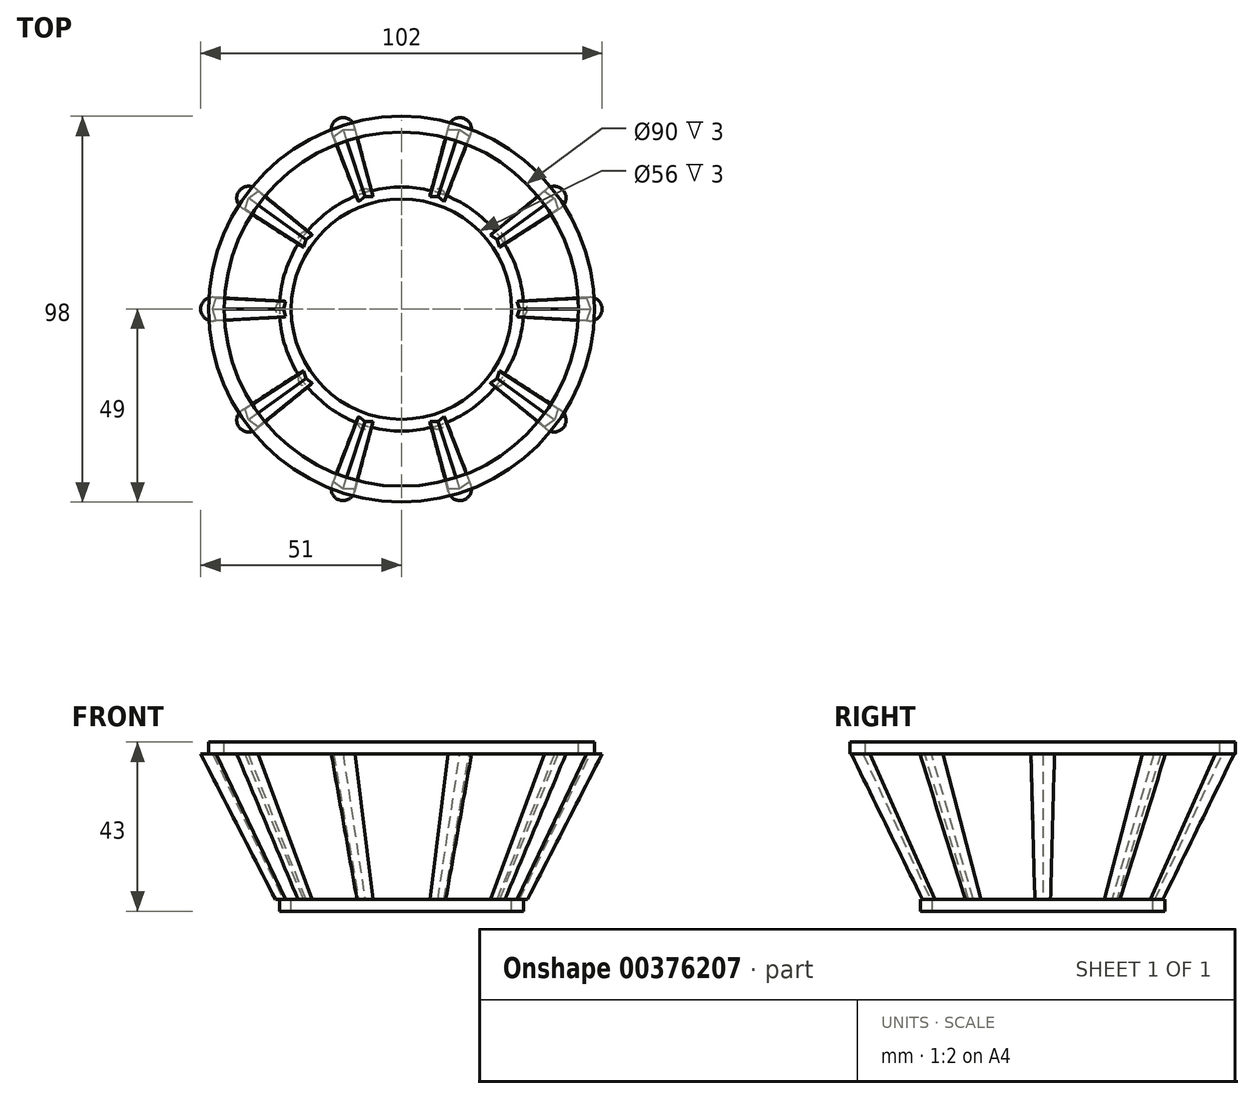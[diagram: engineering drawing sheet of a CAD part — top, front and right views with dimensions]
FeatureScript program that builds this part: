
annotation { "Feature Type Name" : "Feature", "Feature Type Description" : "" }
export const myFeature = defineFeature(function(context is Context, id is Id, definition is map)
    precondition{}
    {
        {
            var Q0;
            Q0=qCreatedBy(makeId("Top.planeOp"),FACE);
            var sketch = newSketch(context, id + "F0", { "sketchPlane" : qUnion([Q0])});
            skCircle(sketch, "E0.cCircle", {"center": v(0, 0) * mm, "radius": 48 * mm, "construction": true});
            skLineSegment(sketch, "E0.0", {"start": v(48, 0) * mm, "end": v(38.83, -28.21) * mm});
            skLineSegment(sketch, "E0.1", {"start": v(38.83, -28.21) * mm, "end": v(14.83, -45.65) * mm});
            skLineSegment(sketch, "E0.2", {"start": v(14.83, -45.65) * mm, "end": v(-14.83, -45.65) * mm});
            skLineSegment(sketch, "E0.3", {"start": v(-14.83, -45.65) * mm, "end": v(-38.83, -28.21) * mm});
            skLineSegment(sketch, "E0.4", {"start": v(-38.83, -28.21) * mm, "end": v(-48, 0) * mm});
            skLineSegment(sketch, "E0.5", {"start": v(-48, 0) * mm, "end": v(-38.83, 28.21) * mm});
            skLineSegment(sketch, "E0.6", {"start": v(-38.83, 28.21) * mm, "end": v(-14.83, 45.65) * mm});
            skLineSegment(sketch, "E0.7", {"start": v(-14.83, 45.65) * mm, "end": v(14.83, 45.65) * mm});
            skLineSegment(sketch, "E0.8", {"start": v(14.83, 45.65) * mm, "end": v(38.83, 28.21) * mm});
            skLineSegment(sketch, "E0.9", {"start": v(38.83, 28.21) * mm, "end": v(48, 0) * mm});
            skCircle(sketch, "E1.0", {"center": v(0, 0) * mm, "radius": 45 * mm});
            skCircle(sketch, "E2.0", {"center": v(0, 0) * mm, "radius": 49 * mm});
            skSolve(sketch);
        }
        {
            var Q0;
            Q0=makeQuery(id+"F0.imprint","IMPRINT",FACE,{"disambiguationData":[TD([[makeQuery(id+"F0.imprint","IMPRINT",EDGE,{"derivedFrom":sQuery(id+"F0.wireOp",EDGE,"E0.0")}),-1.0]])]});
            extrude(context, id + "F1", {"entities" : qUnion([Q0]), "oppositeDirection" : true, "depth" : 3 * mm, "offsetDistance" : 25 * mm});
        }
        {
            var Q0;
            Q0=makeQuery(id+"F1.opExtrude","CAP_FACE",FACE,{"disambiguationData":[OSD([sQuery(id+"F0.wireOp",EDGE,"E0.0"),sQuery(id+"F0.wireOp",EDGE,"E0.1"),sQuery(id+"F0.wireOp",EDGE,"E0.2"),sQuery(id+"F0.wireOp",EDGE,"E0.3"),sQuery(id+"F0.wireOp",EDGE,"E0.4"),sQuery(id+"F0.wireOp",EDGE,"E0.5"),sQuery(id+"F0.wireOp",EDGE,"E0.6"),sQuery(id+"F0.wireOp",EDGE,"E0.7"),sQuery(id+"F0.wireOp",EDGE,"E0.8"),sQuery(id+"F0.wireOp",EDGE,"E0.9"),sQuery(id+"F0.wireOp",EDGE,"E1.0")])],"isStart":false});
            var sketch = newSketch(context, id + "F2", { "sketchPlane" : qUnion([Q0])});
            skCircle(sketch, "E3", {"center": v(-38.83, -28.21) * mm, "radius": 3 * mm});
            skCircle(sketch, "E4", {"center": v(-14.83, -45.65) * mm, "radius": 3 * mm});
            skCircle(sketch, "E5", {"center": v(14.83, -45.65) * mm, "radius": 3 * mm});
            skCircle(sketch, "E6", {"center": v(38.83, -28.21) * mm, "radius": 3 * mm});
            skCircle(sketch, "E7", {"center": v(48, 0) * mm, "radius": 3 * mm});
            skCircle(sketch, "E8", {"center": v(38.83, 28.21) * mm, "radius": 3 * mm});
            skCircle(sketch, "E9", {"center": v(14.83, 45.65) * mm, "radius": 3 * mm});
            skCircle(sketch, "E10", {"center": v(-14.83, 45.65) * mm, "radius": 3 * mm});
            skCircle(sketch, "E11", {"center": v(-38.83, 28.21) * mm, "radius": 3 * mm});
            skCircle(sketch, "E12", {"center": v(-48, 0) * mm, "radius": 3 * mm});
            skCircle(sketch, "E13", {"center": v(-26.83, -36.93) * mm, "radius": 3 * mm});
            skCircle(sketch, "E14.1.0", {"center": v(0, -45.65) * mm, "radius": 3 * mm});
            skCircle(sketch, "E14.2.0", {"center": v(26.83, -36.93) * mm, "radius": 3 * mm});
            skCircle(sketch, "E14.3.0", {"center": v(43.42, -14.1) * mm, "radius": 3 * mm});
            skCircle(sketch, "E14.4.0", {"center": v(43.42, 14.1) * mm, "radius": 3 * mm});
            skCircle(sketch, "E14.5.0", {"center": v(26.83, 36.93) * mm, "radius": 3 * mm});
            skCircle(sketch, "E14.6.0", {"center": v(0, 45.65) * mm, "radius": 3 * mm});
            skCircle(sketch, "E14.7.0", {"center": v(-26.83, 36.93) * mm, "radius": 3 * mm});
            skCircle(sketch, "E14.8.0", {"center": v(-43.42, 14.1) * mm, "radius": 3 * mm});
            skCircle(sketch, "E14.9.0", {"center": v(-43.42, -14.1) * mm, "radius": 3 * mm});
            skPoint(sketch, "E14.center", {"position": v(0, 0) * mm});
            skSolve(sketch);
        }
        {
            var Q0;
            Q0=makeQuery(id+"F0.imprint","IMPRINT",FACE,{"disambiguationData":[TD([[makeQuery(id+"F0.imprint","IMPRINT",EDGE,{"derivedFrom":sQuery(id+"F0.wireOp",EDGE,"E0.0")}),1.0]])]});
            extrude(context, id + "F3", {"entities" : qUnion([Q0]), "operationType" : NewBodyOperationType.ADD, "oppositeDirection" : true, "depth" : 3 * mm, "offsetDistance" : 25 * mm});
        }
        {
            var Q0;
            Q0=qCreatedBy(makeId("Top.planeOp"),FACE);
            cPlane(context, id + "F4", {"entities" : qUnion([Q0]), "cplaneType" : CPlaneType.OFFSET, "offset" : 40 * mm, "oppositeDirection" : true, "width" : 150 * mm, "height" : 150 * mm});
        }
        {
            var Q0;
            Q0=qCreatedBy(id+"F4.planeOp",FACE);
            var sketch = newSketch(context, id + "F5", { "sketchPlane" : qUnion([Q0])});
            skCircle(sketch, "E15.cCircle", {"center": v(0, 0) * mm, "radius": 30 * mm, "construction": true});
            skLineSegment(sketch, "E15.0", {"start": v(30, 0) * mm, "end": v(24.27, -17.63) * mm});
            skLineSegment(sketch, "E15.1", {"start": v(24.27, -17.63) * mm, "end": v(9.27, -28.53) * mm});
            skLineSegment(sketch, "E15.2", {"start": v(9.27, -28.53) * mm, "end": v(-9.27, -28.53) * mm});
            skLineSegment(sketch, "E15.3", {"start": v(-9.27, -28.53) * mm, "end": v(-24.27, -17.63) * mm});
            skLineSegment(sketch, "E15.4", {"start": v(-24.27, -17.63) * mm, "end": v(-30, 0) * mm});
            skLineSegment(sketch, "E15.5", {"start": v(-30, 0) * mm, "end": v(-24.27, 17.63) * mm});
            skLineSegment(sketch, "E15.6", {"start": v(-24.27, 17.63) * mm, "end": v(-9.27, 28.53) * mm});
            skLineSegment(sketch, "E15.7", {"start": v(-9.27, 28.53) * mm, "end": v(9.27, 28.53) * mm});
            skLineSegment(sketch, "E15.8", {"start": v(9.27, 28.53) * mm, "end": v(24.27, 17.63) * mm});
            skLineSegment(sketch, "E15.9", {"start": v(24.27, 17.63) * mm, "end": v(30, 0) * mm});
            skCircle(sketch, "E16.0", {"center": v(0, 0) * mm, "radius": 28 * mm});
            skCircle(sketch, "E17.0", {"center": v(0, 0) * mm, "radius": 31 * mm});
            skSolve(sketch);
        }
        {
            var Q0;
            Q0=makeQuery(id+"F5.imprint","IMPRINT",FACE,{"disambiguationData":[TD([[makeQuery(id+"F5.imprint","IMPRINT",EDGE,{"derivedFrom":sQuery(id+"F5.wireOp",EDGE,"E15.0")}),-1.0]])]});
            extrude(context, id + "F6", {"entities" : qUnion([Q0]), "oppositeDirection" : true, "depth" : 3 * mm, "offsetDistance" : 25 * mm});
        }
        {
            var Q0;
            Q0=makeQuery(id+"F6.opExtrude","CAP_FACE",FACE,{"disambiguationData":[OSD([sQuery(id+"F5.wireOp",EDGE,"E15.0"),sQuery(id+"F5.wireOp",EDGE,"E15.1"),sQuery(id+"F5.wireOp",EDGE,"E15.2"),sQuery(id+"F5.wireOp",EDGE,"E15.3"),sQuery(id+"F5.wireOp",EDGE,"E15.4"),sQuery(id+"F5.wireOp",EDGE,"E15.5"),sQuery(id+"F5.wireOp",EDGE,"E15.6"),sQuery(id+"F5.wireOp",EDGE,"E15.7"),sQuery(id+"F5.wireOp",EDGE,"E15.8"),sQuery(id+"F5.wireOp",EDGE,"E15.9"),sQuery(id+"F5.wireOp",EDGE,"E16.0")])],"isStart":true});
            var sketch = newSketch(context, id + "F7", { "sketchPlane" : qUnion([Q0])});
            skCircle(sketch, "E18", {"center": v(-24.27, -17.63) * mm, "radius": 2 * mm});
            skCircle(sketch, "E19", {"center": v(-16.77, -23.08) * mm, "radius": 2 * mm});
            skCircle(sketch, "E20.1.0", {"center": v(0, -28.53) * mm, "radius": 2 * mm});
            skCircle(sketch, "E20.2.0", {"center": v(16.77, -23.08) * mm, "radius": 2 * mm});
            skCircle(sketch, "E20.3.0", {"center": v(27.14, -8.82) * mm, "radius": 2 * mm});
            skCircle(sketch, "E20.4.0", {"center": v(27.14, 8.82) * mm, "radius": 2 * mm});
            skCircle(sketch, "E20.5.0", {"center": v(16.77, 23.08) * mm, "radius": 2 * mm});
            skCircle(sketch, "E20.6.0", {"center": v(0, 28.53) * mm, "radius": 2 * mm});
            skCircle(sketch, "E20.7.0", {"center": v(-16.77, 23.08) * mm, "radius": 2 * mm});
            skCircle(sketch, "E20.8.0", {"center": v(-27.14, 8.82) * mm, "radius": 2 * mm});
            skCircle(sketch, "E20.9.0", {"center": v(-27.14, -8.82) * mm, "radius": 2 * mm});
            skPoint(sketch, "E20.center", {"position": v(0, 0) * mm});
            skCircle(sketch, "E21.1.0", {"center": v(-9.27, -28.53) * mm, "radius": 2 * mm});
            skCircle(sketch, "E21.2.0", {"center": v(9.27, -28.53) * mm, "radius": 2 * mm});
            skCircle(sketch, "E21.3.0", {"center": v(24.27, -17.63) * mm, "radius": 2 * mm});
            skCircle(sketch, "E21.4.0", {"center": v(30, 0) * mm, "radius": 2 * mm});
            skCircle(sketch, "E21.5.0", {"center": v(24.27, 17.63) * mm, "radius": 2 * mm});
            skCircle(sketch, "E21.6.0", {"center": v(9.27, 28.53) * mm, "radius": 2 * mm});
            skCircle(sketch, "E21.7.0", {"center": v(-9.27, 28.53) * mm, "radius": 2 * mm});
            skCircle(sketch, "E21.8.0", {"center": v(-24.27, 17.63) * mm, "radius": 2 * mm});
            skCircle(sketch, "E21.9.0", {"center": v(-30, 0) * mm, "radius": 2 * mm});
            skSolve(sketch);
        }
        {
            var Q0;
            Q0=makeQuery(id+"F5.imprint","IMPRINT",FACE,{"disambiguationData":[TD([[makeQuery(id+"F5.imprint","IMPRINT",EDGE,{"derivedFrom":sQuery(id+"F5.wireOp",EDGE,"E15.0")}),1.0]])]});
            extrude(context, id + "F8", {"entities" : qUnion([Q0]), "operationType" : NewBodyOperationType.ADD, "oppositeDirection" : true, "depth" : 3 * mm, "offsetDistance" : 25 * mm});
        }
        {
            var Q1;
            {var subQ0=sQuery(id+"F2.wireOp",EDGE,"E12");var subQ1=makeQuery(id+"F1.opExtrude","CAP_EDGE",EDGE,{"disambiguationData":[OSD([sQuery(id+"F0.wireOp",EDGE,"E0.4")])],"isStart":false});var subQ2=makeQuery(id+"F2.imprint","INTERSECT",VERTEX,{"derivedFrom":[subQ1,subQ0]});Q1=makeQuery(id+"F2.imprint","IMPRINT",FACE,{"disambiguationData":[TD([[makeQuery(id+"F2.imprint","IMPRINT",EDGE,{"disambiguationData":[TD([[subQ2,-1.0]])],"derivedFrom":subQ0}),1.0]])]});}
            var Q2;
            {var subQ0=sQuery(id+"F7.wireOp",EDGE,"E21.9.0");var subQ1=makeQuery(id+"F6.opExtrude","CAP_EDGE",EDGE,{"disambiguationData":[OSD([sQuery(id+"F5.wireOp",EDGE,"E15.5")])],"isStart":true});var subQ2=makeQuery(id+"F7.imprint","INTERSECT",VERTEX,{"derivedFrom":[subQ1,subQ0]});Q2=makeQuery(id+"F7.imprint","IMPRINT",FACE,{"disambiguationData":[TD([[makeQuery(id+"F7.imprint","IMPRINT",EDGE,{"disambiguationData":[TD([[subQ2,-1.0]])],"derivedFrom":subQ0}),1.0]])]});}
            loft(context, id + "F9", {"operationType" : NewBodyOperationType.ADD, "sheetProfilesArray" : [{ "sheetProfileEntities" : qUnion([Q1]) }, { "sheetProfileEntities" : qUnion([Q2]) }]});
        }
        {
            var Q0;
            {var subQ0=sQuery(id+"F7.wireOp",EDGE,"E18");var subQ1=makeQuery(id+"F6.opExtrude","CAP_EDGE",EDGE,{"disambiguationData":[OSD([sQuery(id+"F5.wireOp",EDGE,"E15.4")])],"isStart":true});var subQ2=makeQuery(id+"F7.imprint","INTERSECT",VERTEX,{"derivedFrom":[subQ1,subQ0]});Q0=makeQuery(id+"F7.imprint","IMPRINT",FACE,{"disambiguationData":[TD([[makeQuery(id+"F7.imprint","IMPRINT",EDGE,{"disambiguationData":[TD([[subQ2,-1.0]])],"derivedFrom":subQ0}),1.0]])]});}
            var Q1;
            {var subQ0=sQuery(id+"F2.wireOp",EDGE,"E11");var subQ1=makeQuery(id+"F1.opExtrude","CAP_EDGE",EDGE,{"disambiguationData":[OSD([sQuery(id+"F0.wireOp",EDGE,"E0.4")])],"isStart":false});var subQ2=makeQuery(id+"F2.imprint","INTERSECT",VERTEX,{"derivedFrom":[subQ1,subQ0]});Q1=makeQuery(id+"F2.imprint","IMPRINT",FACE,{"disambiguationData":[TD([[makeQuery(id+"F2.imprint","IMPRINT",EDGE,{"disambiguationData":[TD([[subQ2,1.0]])],"derivedFrom":subQ0}),1.0]])]});}
            loft(context, id + "F10", {"operationType" : NewBodyOperationType.ADD, "sheetProfilesArray" : [{ "sheetProfileEntities" : qUnion([Q0]) }, { "sheetProfileEntities" : qUnion([Q1]) }]});
        }
        {
            var Q0;
            {var subQ0=sQuery(id+"F2.wireOp",EDGE,"E10");var subQ1=makeQuery(id+"F1.opExtrude","CAP_EDGE",EDGE,{"disambiguationData":[OSD([sQuery(id+"F0.wireOp",EDGE,"E0.3")])],"isStart":false});var subQ2=makeQuery(id+"F2.imprint","INTERSECT",VERTEX,{"derivedFrom":[subQ1,subQ0]});Q0=makeQuery(id+"F2.imprint","IMPRINT",FACE,{"disambiguationData":[TD([[makeQuery(id+"F2.imprint","IMPRINT",EDGE,{"disambiguationData":[TD([[subQ2,1.0]])],"derivedFrom":subQ0}),1.0]])]});}
            var Q1;
            {var subQ0=sQuery(id+"F7.wireOp",EDGE,"E21.1.0");var subQ1=makeQuery(id+"F6.opExtrude","CAP_EDGE",EDGE,{"disambiguationData":[OSD([sQuery(id+"F5.wireOp",EDGE,"E15.3")])],"isStart":true});var subQ2=makeQuery(id+"F7.imprint","INTERSECT",VERTEX,{"derivedFrom":[subQ1,subQ0]});Q1=makeQuery(id+"F7.imprint","IMPRINT",FACE,{"disambiguationData":[TD([[makeQuery(id+"F7.imprint","IMPRINT",EDGE,{"disambiguationData":[TD([[subQ2,-1.0]])],"derivedFrom":subQ0}),1.0]])]});}
            loft(context, id + "F11", {"operationType" : NewBodyOperationType.ADD, "sheetProfilesArray" : [{ "sheetProfileEntities" : qUnion([Q0]) }, { "sheetProfileEntities" : qUnion([Q1]) }]});
        }
        {
            var Q0;
            {var subQ0=sQuery(id+"F7.wireOp",EDGE,"E21.2.0");var subQ1=makeQuery(id+"F6.opExtrude","CAP_EDGE",EDGE,{"disambiguationData":[OSD([sQuery(id+"F5.wireOp",EDGE,"E15.2")])],"isStart":true});var subQ2=makeQuery(id+"F7.imprint","INTERSECT",VERTEX,{"derivedFrom":[subQ1,subQ0]});Q0=makeQuery(id+"F7.imprint","IMPRINT",FACE,{"disambiguationData":[TD([[makeQuery(id+"F7.imprint","IMPRINT",EDGE,{"disambiguationData":[TD([[subQ2,-1.0]])],"derivedFrom":subQ0}),1.0]])]});}
            var Q1;
            {var subQ0=sQuery(id+"F2.wireOp",EDGE,"E9");var subQ1=makeQuery(id+"F1.opExtrude","CAP_EDGE",EDGE,{"disambiguationData":[OSD([sQuery(id+"F0.wireOp",EDGE,"E0.2")])],"isStart":false});var subQ2=makeQuery(id+"F2.imprint","INTERSECT",VERTEX,{"derivedFrom":[subQ1,subQ0]});Q1=makeQuery(id+"F2.imprint","IMPRINT",FACE,{"disambiguationData":[TD([[makeQuery(id+"F2.imprint","IMPRINT",EDGE,{"disambiguationData":[TD([[subQ2,1.0]])],"derivedFrom":subQ0}),1.0]])]});}
            loft(context, id + "F12", {"operationType" : NewBodyOperationType.ADD, "sheetProfilesArray" : [{ "sheetProfileEntities" : qUnion([Q0]) }, { "sheetProfileEntities" : qUnion([Q1]) }]});
        }
        {
            var Q0;
            {var subQ0=sQuery(id+"F2.wireOp",EDGE,"E8");var subQ1=makeQuery(id+"F1.opExtrude","CAP_EDGE",EDGE,{"disambiguationData":[OSD([sQuery(id+"F0.wireOp",EDGE,"E0.1")])],"isStart":false});var subQ2=makeQuery(id+"F2.imprint","INTERSECT",VERTEX,{"derivedFrom":[subQ1,subQ0]});Q0=makeQuery(id+"F2.imprint","IMPRINT",FACE,{"disambiguationData":[TD([[makeQuery(id+"F2.imprint","IMPRINT",EDGE,{"disambiguationData":[TD([[subQ2,1.0]])],"derivedFrom":subQ0}),1.0]])]});}
            var Q1;
            {var subQ0=sQuery(id+"F7.wireOp",EDGE,"E21.3.0");var subQ1=makeQuery(id+"F6.opExtrude","CAP_EDGE",EDGE,{"disambiguationData":[OSD([sQuery(id+"F5.wireOp",EDGE,"E15.1")])],"isStart":true});var subQ2=makeQuery(id+"F7.imprint","INTERSECT",VERTEX,{"derivedFrom":[subQ1,subQ0]});Q1=makeQuery(id+"F7.imprint","IMPRINT",FACE,{"disambiguationData":[TD([[makeQuery(id+"F7.imprint","IMPRINT",EDGE,{"disambiguationData":[TD([[subQ2,-1.0]])],"derivedFrom":subQ0}),1.0]])]});}
            loft(context, id + "F13", {"operationType" : NewBodyOperationType.ADD, "sheetProfilesArray" : [{ "sheetProfileEntities" : qUnion([Q0]) }, { "sheetProfileEntities" : qUnion([Q1]) }]});
        }
        {
            var Q0;
            {var subQ0=sQuery(id+"F7.wireOp",EDGE,"E21.4.0");var subQ1=makeQuery(id+"F6.opExtrude","CAP_EDGE",EDGE,{"disambiguationData":[OSD([sQuery(id+"F5.wireOp",EDGE,"E15.0")])],"isStart":true});var subQ2=makeQuery(id+"F7.imprint","INTERSECT",VERTEX,{"derivedFrom":[subQ1,subQ0]});Q0=makeQuery(id+"F7.imprint","IMPRINT",FACE,{"disambiguationData":[TD([[makeQuery(id+"F7.imprint","IMPRINT",EDGE,{"disambiguationData":[TD([[subQ2,-1.0]])],"derivedFrom":subQ0}),1.0]])]});}
            var Q1;
            {var subQ0=sQuery(id+"F2.wireOp",EDGE,"E7");var subQ1=makeQuery(id+"F1.opExtrude","CAP_EDGE",EDGE,{"disambiguationData":[OSD([sQuery(id+"F0.wireOp",EDGE,"E0.0")])],"isStart":false});var subQ2=makeQuery(id+"F2.imprint","INTERSECT",VERTEX,{"derivedFrom":[subQ1,subQ0]});Q1=makeQuery(id+"F2.imprint","IMPRINT",FACE,{"disambiguationData":[TD([[makeQuery(id+"F2.imprint","IMPRINT",EDGE,{"disambiguationData":[TD([[subQ2,1.0]])],"derivedFrom":subQ0}),1.0]])]});}
            loft(context, id + "F14", {"operationType" : NewBodyOperationType.ADD, "sheetProfilesArray" : [{ "sheetProfileEntities" : qUnion([Q0]) }, { "sheetProfileEntities" : qUnion([Q1]) }]});
        }
        {
            var Q0;
            {var subQ0=sQuery(id+"F2.wireOp",EDGE,"E6");var subQ1=makeQuery(id+"F1.opExtrude","CAP_EDGE",EDGE,{"disambiguationData":[OSD([sQuery(id+"F0.wireOp",EDGE,"E0.9")])],"isStart":false});var subQ2=makeQuery(id+"F2.imprint","INTERSECT",VERTEX,{"derivedFrom":[subQ1,subQ0]});Q0=makeQuery(id+"F2.imprint","IMPRINT",FACE,{"disambiguationData":[TD([[makeQuery(id+"F2.imprint","IMPRINT",EDGE,{"disambiguationData":[TD([[subQ2,1.0]])],"derivedFrom":subQ0}),1.0]])]});}
            var Q1;
            {var subQ0=sQuery(id+"F7.wireOp",EDGE,"E21.5.0");var subQ1=makeQuery(id+"F6.opExtrude","CAP_EDGE",EDGE,{"disambiguationData":[OSD([sQuery(id+"F5.wireOp",EDGE,"E15.9")])],"isStart":true});var subQ2=makeQuery(id+"F7.imprint","INTERSECT",VERTEX,{"derivedFrom":[subQ1,subQ0]});Q1=makeQuery(id+"F7.imprint","IMPRINT",FACE,{"disambiguationData":[TD([[makeQuery(id+"F7.imprint","IMPRINT",EDGE,{"disambiguationData":[TD([[subQ2,-1.0]])],"derivedFrom":subQ0}),1.0]])]});}
            loft(context, id + "F15", {"operationType" : NewBodyOperationType.ADD, "sheetProfilesArray" : [{ "sheetProfileEntities" : qUnion([Q0]) }, { "sheetProfileEntities" : qUnion([Q1]) }]});
        }
        {
            var Q0;
            {var subQ0=sQuery(id+"F7.wireOp",EDGE,"E21.6.0");var subQ1=makeQuery(id+"F6.opExtrude","CAP_EDGE",EDGE,{"disambiguationData":[OSD([sQuery(id+"F5.wireOp",EDGE,"E15.8")])],"isStart":true});var subQ2=makeQuery(id+"F7.imprint","INTERSECT",VERTEX,{"derivedFrom":[subQ1,subQ0]});Q0=makeQuery(id+"F7.imprint","IMPRINT",FACE,{"disambiguationData":[TD([[makeQuery(id+"F7.imprint","IMPRINT",EDGE,{"disambiguationData":[TD([[subQ2,-1.0]])],"derivedFrom":subQ0}),1.0]])]});}
            var Q1;
            {var subQ0=sQuery(id+"F2.wireOp",EDGE,"E5");var subQ1=makeQuery(id+"F1.opExtrude","CAP_EDGE",EDGE,{"disambiguationData":[OSD([sQuery(id+"F0.wireOp",EDGE,"E0.8")])],"isStart":false});var subQ2=makeQuery(id+"F2.imprint","INTERSECT",VERTEX,{"derivedFrom":[subQ1,subQ0]});Q1=makeQuery(id+"F2.imprint","IMPRINT",FACE,{"disambiguationData":[TD([[makeQuery(id+"F2.imprint","IMPRINT",EDGE,{"disambiguationData":[TD([[subQ2,1.0]])],"derivedFrom":subQ0}),1.0]])]});}
            loft(context, id + "F16", {"operationType" : NewBodyOperationType.ADD, "sheetProfilesArray" : [{ "sheetProfileEntities" : qUnion([Q0]) }, { "sheetProfileEntities" : qUnion([Q1]) }]});
        }
        {
            var Q0;
            {var subQ0=sQuery(id+"F2.wireOp",EDGE,"E4");var subQ1=makeQuery(id+"F1.opExtrude","CAP_EDGE",EDGE,{"disambiguationData":[OSD([sQuery(id+"F0.wireOp",EDGE,"E0.7")])],"isStart":false});var subQ2=makeQuery(id+"F2.imprint","INTERSECT",VERTEX,{"derivedFrom":[subQ1,subQ0]});Q0=makeQuery(id+"F2.imprint","IMPRINT",FACE,{"disambiguationData":[TD([[makeQuery(id+"F2.imprint","IMPRINT",EDGE,{"disambiguationData":[TD([[subQ2,1.0]])],"derivedFrom":subQ0}),1.0]])]});}
            var Q1;
            {var subQ0=sQuery(id+"F7.wireOp",EDGE,"E21.7.0");var subQ1=makeQuery(id+"F6.opExtrude","CAP_EDGE",EDGE,{"disambiguationData":[OSD([sQuery(id+"F5.wireOp",EDGE,"E15.7")])],"isStart":true});var subQ2=makeQuery(id+"F7.imprint","INTERSECT",VERTEX,{"derivedFrom":[subQ1,subQ0]});Q1=makeQuery(id+"F7.imprint","IMPRINT",FACE,{"disambiguationData":[TD([[makeQuery(id+"F7.imprint","IMPRINT",EDGE,{"disambiguationData":[TD([[subQ2,-1.0]])],"derivedFrom":subQ0}),1.0]])]});}
            loft(context, id + "F17", {"operationType" : NewBodyOperationType.ADD, "sheetProfilesArray" : [{ "sheetProfileEntities" : qUnion([Q0]) }, { "sheetProfileEntities" : qUnion([Q1]) }]});
        }
        {
            var Q0;
            {var subQ0=sQuery(id+"F7.wireOp",EDGE,"E21.8.0");var subQ1=makeQuery(id+"F6.opExtrude","CAP_EDGE",EDGE,{"disambiguationData":[OSD([sQuery(id+"F5.wireOp",EDGE,"E15.6")])],"isStart":true});var subQ2=makeQuery(id+"F7.imprint","INTERSECT",VERTEX,{"derivedFrom":[subQ1,subQ0]});Q0=makeQuery(id+"F7.imprint","IMPRINT",FACE,{"disambiguationData":[TD([[makeQuery(id+"F7.imprint","IMPRINT",EDGE,{"disambiguationData":[TD([[subQ2,-1.0]])],"derivedFrom":subQ0}),1.0]])]});}
            var Q1;
            {var subQ0=sQuery(id+"F2.wireOp",EDGE,"E3");var subQ1=makeQuery(id+"F1.opExtrude","CAP_EDGE",EDGE,{"disambiguationData":[OSD([sQuery(id+"F0.wireOp",EDGE,"E0.5")])],"isStart":false});var subQ2=makeQuery(id+"F2.imprint","INTERSECT",VERTEX,{"derivedFrom":[subQ1,subQ0]});Q1=makeQuery(id+"F2.imprint","IMPRINT",FACE,{"disambiguationData":[TD([[makeQuery(id+"F2.imprint","IMPRINT",EDGE,{"disambiguationData":[TD([[subQ2,-1.0]])],"derivedFrom":subQ0}),1.0]])]});}
            loft(context, id + "F18", {"operationType" : NewBodyOperationType.ADD, "sheetProfilesArray" : [{ "sheetProfileEntities" : qUnion([Q0]) }, { "sheetProfileEntities" : qUnion([Q1]) }]});
        }
    });
